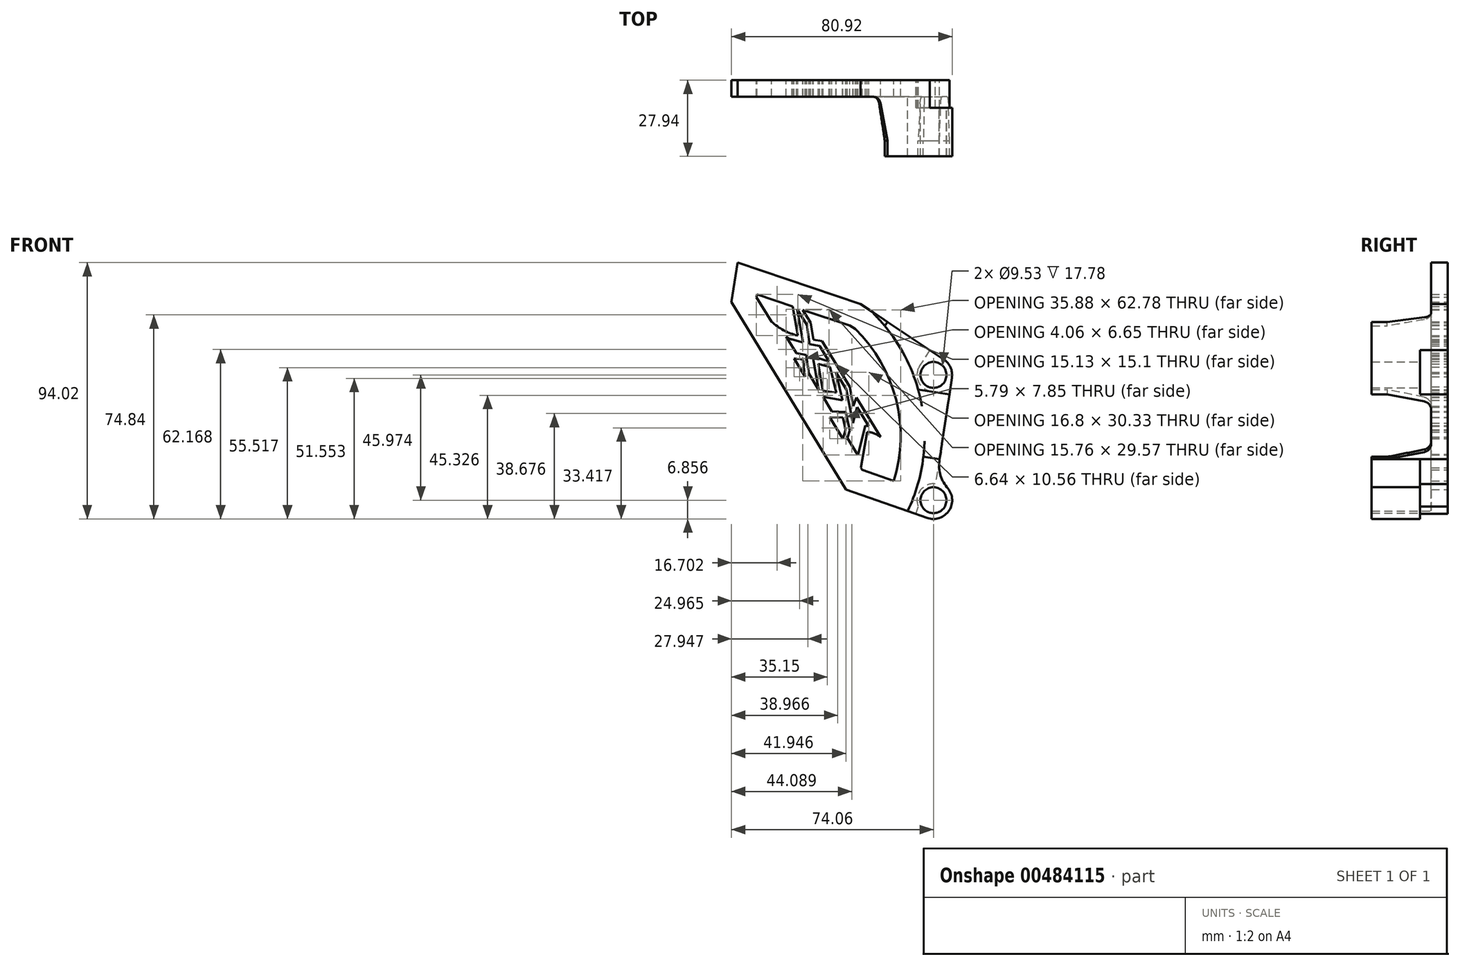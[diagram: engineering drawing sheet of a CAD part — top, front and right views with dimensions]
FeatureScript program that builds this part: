
annotation { "Feature Type Name" : "Feature", "Feature Type Description" : "" }
export const myFeature = defineFeature(function(context is Context, id is Id, definition is map)
    precondition{}
    {
        {
            var Q0;
            Q0=qCreatedBy(makeId("Front.planeOp"),FACE);
            var sketch = newSketch(context, id + "F0", { "sketchPlane" : qUnion([Q0])});
            skCircle(sketch, "E0", {"center": v(0, 0) * mm, "radius": 4.76 * mm});
            skLineSegment(sketch, "E1", {"start": v(0, 40.2) * mm, "end": v(0, -100.93) * mm, "construction": true});
            skCircle(sketch, "E2", {"center": v(0, -45.97) * mm, "radius": 4.76 * mm});
            skCircle(sketch, "E3", {"center": v(0, 0) * mm, "radius": 6.86 * mm});
            skCircle(sketch, "E4", {"center": v(0, -45.97) * mm, "radius": 6.86 * mm});
            skLineSegment(sketch, "E5", {"start": v(0, -45.97) * mm, "end": v(6.94, 0) * mm});
            skLineSegment(sketch, "E6", {"start": v(-32.02, -42.07) * mm, "end": v(-74.06, 26.75) * mm});
            skLineSegment(sketch, "E7", {"start": v(-74.06, 26.75) * mm, "end": v(-71.88, 41.2) * mm});
            skLineSegment(sketch, "E8", {"start": v(-71.88, 41.2) * mm, "end": v(-26.74, 26.02) * mm});
            skArc(sketch, "E9", {"start": v(2.27, -30.95) * mm, "mid": v(2.46, -36.33) * mm, "end": v(4.88, -41.15) * mm});
            skArc(sketch, "E10", {"start": v(-9.46, -49.94) * mm, "mid": v(-4.33, -10.9) * mm, "end": v(-23.2, 23.67) * mm});
            skLineSegment(sketch, "E11", {"start": v(-32.02, -42.07) * mm, "end": v(-9.46, -49.94) * mm});
            skLineSegment(sketch, "E12", {"start": v(-9.46, -49.94) * mm, "end": v(-2.26, -52.45) * mm});
            skLineSegment(sketch, "E13", {"start": v(-26.74, 26.02) * mm, "end": v(-23.2, 23.67) * mm});
            skLineSegment(sketch, "E14", {"start": v(-23.2, 23.67) * mm, "end": v(3.8, 5.71) * mm});
            skLineSegment(sketch, "E15.0", {"start": v(-64.78, 29.56) * mm, "end": v(-30.63, 18.08) * mm});
            skArc(sketch, "E15.1", {"start": v(-14.5, -38.9) * mm, "mid": v(-13.7, -9.04) * mm, "end": v(-28.7, 16.8) * mm});
            skLineSegment(sketch, "E15.2", {"start": v(-26.18, -34.83) * mm, "end": v(-14.5, -38.9) * mm});
            skLineSegment(sketch, "E15.3", {"start": v(-30.63, 18.08) * mm, "end": v(-28.7, 16.8) * mm});
            skLineSegment(sketch, "E15.4", {"start": v(-26.18, -34.83) * mm, "end": v(-64.92, 28.6) * mm});
            skLineSegment(sketch, "E15.5", {"start": v(-64.92, 28.6) * mm, "end": v(-64.78, 29.56) * mm});
            skLineSegment(sketch, "E16.MirrorCS", {"start": v(-27.72, -29.32) * mm, "end": v(-27.63, -29.13) * mm});
            skLineSegment(sketch, "E17.MirrorCS", {"start": v(-25, -18.52) * mm, "end": v(-23.71, -18.84) * mm});
            skLineSegment(sketch, "E18.MirrorCS", {"start": v(-45.43, 11.33) * mm, "end": v(-41.72, 10.68) * mm});
            skLineSegment(sketch, "E19.MirrorCS", {"start": v(-30.66, -20.33) * mm, "end": v(-31.52, -23.1) * mm});
            skLineSegment(sketch, "E20.MirrorCS", {"start": v(-32.2, -20.1) * mm, "end": v(-33.2, -23.37) * mm});
            skLineSegment(sketch, "E21.MirrorCS", {"start": v(-51.14, 6.01) * mm, "end": v(-47.98, 5.65) * mm});
            skArc(sketch, "E22.MirrorCS", {"start": v(-51.91, 13.03) * mm, "mid": v(-53.03, 13.4) * mm, "end": v(-54, 14.07) * mm});
            skLineSegment(sketch, "E23.MirrorCS", {"start": v(-28.25, -8.33) * mm, "end": v(-29.44, -11.4) * mm});
            skLineSegment(sketch, "E24.MirrorCS", {"start": v(-40.9, 12.41) * mm, "end": v(-43.99, 12.95) * mm});
            skLineSegment(sketch, "E25.MirrorCS", {"start": v(-46.67, 7.38) * mm, "end": v(-50.3, 8.01) * mm});
            skLineSegment(sketch, "E26.MirrorCS", {"start": v(-37.87, 2.87) * mm, "end": v(-35.6, -6.56) * mm});
            skLineSegment(sketch, "E27.MirrorCS", {"start": v(-47.98, 5.65) * mm, "end": v(-47.06, -0.67) * mm});
            skLineSegment(sketch, "E28.MirrorCS", {"start": v(-46.45, 18.37) * mm, "end": v(-45.43, 11.33) * mm});
            skLineSegment(sketch, "E29.MirrorCS", {"start": v(-32.26, -13.6) * mm, "end": v(-30.66, -20.33) * mm});
            skLineSegment(sketch, "E30.MirrorCS", {"start": v(-27.63, -29.13) * mm, "end": v(-25, -18.52) * mm});
            skLineSegment(sketch, "E31.MirrorCS", {"start": v(-42.23, 4) * mm, "end": v(-37.87, 2.87) * mm});
            skLineSegment(sketch, "E32.MirrorCS", {"start": v(-42.08, -5.45) * mm, "end": v(-45.66, 0.43) * mm});
            skLineSegment(sketch, "E33.MirrorCS", {"start": v(-37.25, -13.39) * mm, "end": v(-32.26, -13.6) * mm});
            skArc(sketch, "E34.MirrorCS", {"start": v(-49.8, 14.46) * mm, "mid": v(-54.93, 16.37) * mm, "end": v(-59.4, 19.55) * mm});
            skLineSegment(sketch, "E35.MirrorCS", {"start": v(-47.06, -0.67) * mm, "end": v(-38.01, -15.49) * mm});
            skLineSegment(sketch, "E36.MirrorCS", {"start": v(-49.96, 24.12) * mm, "end": v(-46.45, 18.37) * mm});
            skLineSegment(sketch, "E37.MirrorCS", {"start": v(-59.4, 19.55) * mm, "end": v(-51.14, 6.01) * mm});
            skLineSegment(sketch, "E38.MirrorCS", {"start": v(-40.51, -8.05) * mm, "end": v(-37.25, -13.39) * mm});
            skLineSegment(sketch, "E39.MirrorCS", {"start": v(-40.56, -5.69) * mm, "end": v(-42.23, 4) * mm});
            skLineSegment(sketch, "E40.MirrorCS", {"start": v(-47.85, 11.95) * mm, "end": v(-49.96, 24.12) * mm});
            skLineSegment(sketch, "E41.MirrorCS", {"start": v(-33.2, -23.37) * mm, "end": v(-26.63, -34.14) * mm});
            skLineSegment(sketch, "E42.MirrorCS", {"start": v(-29.6, -17.7) * mm, "end": v(-31.96, -5.33) * mm});
            skLineSegment(sketch, "E43.MirrorCS", {"start": v(-29.44, -11.4) * mm, "end": v(-30.7, -4.32) * mm});
            skLineSegment(sketch, "E44.MirrorCS", {"start": v(-52.81, 31.92) * mm, "end": v(-49.8, 14.46) * mm});
            skLineSegment(sketch, "E45.MirrorCS", {"start": v(-35.83, 1) * mm, "end": v(-33.34, -9.3) * mm});
            skLineSegment(sketch, "E46.MirrorCS", {"start": v(-41.72, 10.68) * mm, "end": v(-38.24, 4.97) * mm});
            skLineSegment(sketch, "E47.MirrorCS", {"start": v(-31.52, -23.1) * mm, "end": v(-27.72, -29.32) * mm});
            skLineSegment(sketch, "E48.MirrorCS", {"start": v(-50.3, 8.01) * mm, "end": v(-54, 14.07) * mm});
            skLineSegment(sketch, "E49.MirrorCS", {"start": v(-23.71, -18.84) * mm, "end": v(-28, -11.8) * mm});
            skLineSegment(sketch, "E50.MirrorCS", {"start": v(-51.91, 13.03) * mm, "end": v(-47.85, 11.95) * mm});
            skLineSegment(sketch, "E51.MirrorCS", {"start": v(-31.96, -5.33) * mm, "end": v(-35.83, 1) * mm});
            skLineSegment(sketch, "E52.MirrorCS", {"start": v(-38.01, -15.49) * mm, "end": v(-33.25, -15.7) * mm});
            skLineSegment(sketch, "E53.MirrorCS", {"start": v(-33.34, -9.3) * mm, "end": v(-40.51, -8.05) * mm});
            skArc(sketch, "E54.MirrorCS", {"start": v(-24.31, -20.94) * mm, "mid": v(-21.7, -21.46) * mm, "end": v(-19.4, -22.82) * mm});
            skLineSegment(sketch, "E55.MirrorCS", {"start": v(-43.99, 12.95) * mm, "end": v(-45.02, 19.15) * mm});
            skLineSegment(sketch, "E56.MirrorCS", {"start": v(-44.27, 6.76) * mm, "end": v(-42.08, -5.45) * mm});
            skLineSegment(sketch, "E57.MirrorCS", {"start": v(-35.6, -6.56) * mm, "end": v(-40.56, -5.69) * mm});
            skLineSegment(sketch, "E58.MirrorCS", {"start": v(-19.4, -22.82) * mm, "end": v(-28.25, -8.33) * mm});
            skLineSegment(sketch, "E59.MirrorCS", {"start": v(-28, -11.8) * mm, "end": v(-29.6, -17.7) * mm});
            skLineSegment(sketch, "E60.MirrorCS", {"start": v(-45.02, 19.15) * mm, "end": v(-52.81, 31.92) * mm});
            skLineSegment(sketch, "E61.MirrorCS", {"start": v(-45.66, 0.43) * mm, "end": v(-46.67, 7.38) * mm});
            skLineSegment(sketch, "E62.MirrorCS", {"start": v(-30.7, -4.32) * mm, "end": v(-40.9, 12.41) * mm});
            skLineSegment(sketch, "E63.MirrorCS", {"start": v(-26.63, -34.14) * mm, "end": v(-24.31, -20.94) * mm});
            skLineSegment(sketch, "E64.MirrorCS", {"start": v(-38.24, 4.97) * mm, "end": v(-44.27, 6.76) * mm});
            skLineSegment(sketch, "E65.MirrorCS", {"start": v(-33.25, -15.7) * mm, "end": v(-32.2, -20.1) * mm});
            skSolve(sketch);
        }
        {
            var Q0;
            Q0=makeQuery(id+"F0.imprint","IMPRINT",FACE,{"disambiguationData":[TD([[makeQuery(id+"F0.imprint","IMPRINT",EDGE,{"derivedFrom":sQuery(id+"F0.wireOp",EDGE,"E6")}),-1.0]])]});
            var Q1;
            {var subQ0=sQuery(id+"F0.wireOp",EDGE,"E44.MirrorCS");var subQ1=sQuery(id+"F0.wireOp",EDGE,"E15.0");var subQ2=makeQuery(id+"F0.imprint","INTERSECT",VERTEX,{"derivedFrom":[subQ1,subQ0]});Q1=makeQuery(id+"F0.imprint","IMPRINT",FACE,{"disambiguationData":[TD([[makeQuery(id+"F0.imprint","IMPRINT",EDGE,{"disambiguationData":[TD([[subQ2,-1.0]])],"derivedFrom":subQ1}),1.0]])]});}
            var Q2;
            Q2=makeQuery(id+"F0.imprint","IMPRINT",FACE,{"disambiguationData":[TD([[makeQuery(id+"F0.imprint","IMPRINT",EDGE,{"derivedFrom":sQuery(id+"F0.wireOp",EDGE,"E16.MirrorCS")}),-1.0]])]});
            var Q3;
            {var subQ5=sQuery(id+"F0.wireOp",EDGE,"E35.MirrorCS");Q3=makeQuery(id+"F0.imprint","IMPRINT",FACE,{"disambiguationData":[TD([[makeQuery(id+"F0.imprint","IMPRINT",EDGE,{"derivedFrom":subQ5}),1.0]])]});}
            var Q4;
            {var subQ5=sQuery(id+"F0.wireOp",EDGE,"E41.MirrorCS");Q4=makeQuery(id+"F0.imprint","IMPRINT",FACE,{"disambiguationData":[TD([[makeQuery(id+"F0.imprint","IMPRINT",EDGE,{"derivedFrom":subQ5}),1.0]])]});}
            var Q5;
            {var subQ0=sQuery(id+"F0.wireOp",EDGE,"E37.MirrorCS");Q5=makeQuery(id+"F0.imprint","IMPRINT",FACE,{"disambiguationData":[TD([[makeQuery(id+"F0.imprint","IMPRINT",EDGE,{"derivedFrom":subQ0}),1.0]])]});}
            extrude(context, id + "F1", {"entities" : qUnion([Q0, Q1, Q2, Q3, Q4, Q5]), "depth" : 6.1 * mm, "offsetDistance" : 25.4 * mm});
        }
        {
            var Q0;
            Q0=makeQuery(id+"F0.imprint","IMPRINT",FACE,{"disambiguationData":[TD([[makeQuery(id+"F0.imprint","IMPRINT",EDGE,{"derivedFrom":sQuery(id+"F0.wireOp",EDGE,"E10")}),-1.0]])]});
            var Q1;
            Q1=makeQuery(id+"F0.imprint","IMPRINT",FACE,{"disambiguationData":[TD([[makeQuery(id+"F0.imprint","IMPRINT",EDGE,{"derivedFrom":sQuery(id+"F0.wireOp",EDGE,"E0")}),-1.0]])]});
            var Q2;
            {var subQ0=sQuery(id+"F0.wireOp",EDGE,"E9");var subQ1=sQuery(id+"F0.wireOp",EDGE,"E4");var subQ2=makeQuery(id+"F0.imprint","INTERSECT",VERTEX,{"derivedFrom":[subQ1,subQ0]});Q2=makeQuery(id+"F0.imprint","IMPRINT",FACE,{"disambiguationData":[TD([[makeQuery(id+"F0.imprint","IMPRINT",EDGE,{"disambiguationData":[TD([[subQ2,-1.0]])],"derivedFrom":subQ1}),-1.0]])]});}
            var Q3;
            Q3=makeQuery(id+"F0.imprint","IMPRINT",FACE,{"disambiguationData":[TD([[makeQuery(id+"F0.imprint","IMPRINT",EDGE,{"derivedFrom":sQuery(id+"F0.wireOp",EDGE,"E2")}),-1.0]])]});
            extrude(context, id + "F2", {"entities" : qUnion([Q0, Q1, Q2, Q3]), "operationType" : NewBodyOperationType.ADD, "depth" : 27.94 * mm, "offsetDistance" : 25.4 * mm});
        }
        {
            var Q0;
            {var subQ0=sQuery(id+"F0.wireOp",EDGE,"E10");Q0=makeQuery(id+"F2.boolean.opBoolean","MERGE",FACE,{"derivedFrom":[makeQuery(id+"F1.opExtrude","CAP_FACE",FACE,{"disambiguationData":[OSD([sQuery(id+"F0.wireOp",EDGE,"E6"),sQuery(id+"F0.wireOp",EDGE,"E7"),sQuery(id+"F0.wireOp",EDGE,"E8"),subQ0,sQuery(id+"F0.wireOp",EDGE,"E11"),sQuery(id+"F0.wireOp",EDGE,"E13"),sQuery(id+"F0.wireOp",EDGE,"E15.0"),sQuery(id+"F0.wireOp",EDGE,"E15.1"),sQuery(id+"F0.wireOp",EDGE,"E15.2"),sQuery(id+"F0.wireOp",EDGE,"E15.3"),sQuery(id+"F0.wireOp",EDGE,"E15.4"),sQuery(id+"F0.wireOp",EDGE,"E15.5"),sQuery(id+"F0.wireOp",EDGE,"E16.MirrorCS"),sQuery(id+"F0.wireOp",EDGE,"E17.MirrorCS"),sQuery(id+"F0.wireOp",EDGE,"E18.MirrorCS"),sQuery(id+"F0.wireOp",EDGE,"E19.MirrorCS"),sQuery(id+"F0.wireOp",EDGE,"E20.MirrorCS"),sQuery(id+"F0.wireOp",EDGE,"E21.MirrorCS"),sQuery(id+"F0.wireOp",EDGE,"E22.MirrorCS"),sQuery(id+"F0.wireOp",EDGE,"E23.MirrorCS"),sQuery(id+"F0.wireOp",EDGE,"E24.MirrorCS"),sQuery(id+"F0.wireOp",EDGE,"E25.MirrorCS"),sQuery(id+"F0.wireOp",EDGE,"E26.MirrorCS"),sQuery(id+"F0.wireOp",EDGE,"E27.MirrorCS"),sQuery(id+"F0.wireOp",EDGE,"E28.MirrorCS"),sQuery(id+"F0.wireOp",EDGE,"E29.MirrorCS"),sQuery(id+"F0.wireOp",EDGE,"E30.MirrorCS"),sQuery(id+"F0.wireOp",EDGE,"E31.MirrorCS"),sQuery(id+"F0.wireOp",EDGE,"E32.MirrorCS"),sQuery(id+"F0.wireOp",EDGE,"E33.MirrorCS"),sQuery(id+"F0.wireOp",EDGE,"E34.MirrorCS"),sQuery(id+"F0.wireOp",EDGE,"E36.MirrorCS"),sQuery(id+"F0.wireOp",EDGE,"E38.MirrorCS"),sQuery(id+"F0.wireOp",EDGE,"E39.MirrorCS"),sQuery(id+"F0.wireOp",EDGE,"E40.MirrorCS"),sQuery(id+"F0.wireOp",EDGE,"E42.MirrorCS"),sQuery(id+"F0.wireOp",EDGE,"E43.MirrorCS"),sQuery(id+"F0.wireOp",EDGE,"E44.MirrorCS"),sQuery(id+"F0.wireOp",EDGE,"E45.MirrorCS"),sQuery(id+"F0.wireOp",EDGE,"E46.MirrorCS"),sQuery(id+"F0.wireOp",EDGE,"E47.MirrorCS"),sQuery(id+"F0.wireOp",EDGE,"E48.MirrorCS"),sQuery(id+"F0.wireOp",EDGE,"E49.MirrorCS"),sQuery(id+"F0.wireOp",EDGE,"E50.MirrorCS"),sQuery(id+"F0.wireOp",EDGE,"E51.MirrorCS"),sQuery(id+"F0.wireOp",EDGE,"E52.MirrorCS"),sQuery(id+"F0.wireOp",EDGE,"E53.MirrorCS"),sQuery(id+"F0.wireOp",EDGE,"E54.MirrorCS"),sQuery(id+"F0.wireOp",EDGE,"E55.MirrorCS"),sQuery(id+"F0.wireOp",EDGE,"E56.MirrorCS"),sQuery(id+"F0.wireOp",EDGE,"E57.MirrorCS"),sQuery(id+"F0.wireOp",EDGE,"E58.MirrorCS"),sQuery(id+"F0.wireOp",EDGE,"E59.MirrorCS"),sQuery(id+"F0.wireOp",EDGE,"E60.MirrorCS"),sQuery(id+"F0.wireOp",EDGE,"E61.MirrorCS"),sQuery(id+"F0.wireOp",EDGE,"E62.MirrorCS"),sQuery(id+"F0.wireOp",EDGE,"E63.MirrorCS"),sQuery(id+"F0.wireOp",EDGE,"E64.MirrorCS"),sQuery(id+"F0.wireOp",EDGE,"E65.MirrorCS")])],"isStart":true}),makeQuery(id+"F2.opExtrude","CAP_FACE",FACE,{"disambiguationData":[OSD([sQuery(id+"F0.wireOp",EDGE,"E0"),sQuery(id+"F0.wireOp",EDGE,"E2"),sQuery(id+"F0.wireOp",EDGE,"E3"),sQuery(id+"F0.wireOp",EDGE,"E4"),sQuery(id+"F0.wireOp",EDGE,"E5"),sQuery(id+"F0.wireOp",EDGE,"E9"),subQ0,sQuery(id+"F0.wireOp",EDGE,"E12"),sQuery(id+"F0.wireOp",EDGE,"E14")])],"isStart":true})]});}
            var sketch = newSketch(context, id + "F3", { "sketchPlane" : qUnion([Q0])});
            skCircle(sketch, "E66", {"center": v(0, 0) * mm, "radius": 6.03 * mm});
            skCircle(sketch, "E67", {"center": v(0, -45.97) * mm, "radius": 6.03 * mm});
            skLineSegment(sketch, "E68", {"start": v(1.37, 9.15) * mm, "end": v(5.1, 3.2) * mm});
            skLineSegment(sketch, "E69", {"start": v(1.37, 9.15) * mm, "end": v(-3.8, 5.71) * mm});
            skLineSegment(sketch, "E70", {"start": v(-5.86, -7.16) * mm, "end": v(1.05, -5.94) * mm});
            skLineSegment(sketch, "E71", {"start": v(-5.86, -7.16) * mm, "end": v(-6.78, -1.02) * mm});
            skLineSegment(sketch, "E72", {"start": v(-2.27, -30.95) * mm, "end": v(-0.65, -39.98) * mm});
            skLineSegment(sketch, "E73", {"start": v(6.46, -50.98) * mm, "end": v(5.55, -48.35) * mm});
            skLineSegment(sketch, "E74", {"start": v(6.46, -50.98) * mm, "end": v(2.26, -52.45) * mm});
            skSolve(sketch);
        }
        {
            var Q0;
            {var subQ0=sQuery(id+"F3.wireOp",EDGE,"E67");Q0=makeQuery(id+"F3.imprint","IMPRINT",FACE,{"disambiguationData":[TD([[makeQuery(id+"F3.imprint","IMPRINT",EDGE,{"disambiguationData":[OD(0.0)],"derivedFrom":subQ0}),-1.0]])]});}
            var Q1;
            {var subQ0=sQuery(id+"F3.wireOp",EDGE,"E66");Q1=makeQuery(id+"F3.imprint","IMPRINT",FACE,{"disambiguationData":[TD([[makeQuery(id+"F3.imprint","IMPRINT",EDGE,{"disambiguationData":[OD(0.0)],"derivedFrom":subQ0}),1.0]])]});}
            var Q2;
            {var subQ2=sQuery(id+"F3.wireOp",EDGE,"E70");Q2=makeQuery(id+"F3.imprint","IMPRINT",FACE,{"disambiguationData":[TD([[makeQuery(id+"F3.imprint","IMPRINT",EDGE,{"derivedFrom":subQ2}),1.0]])]});}
            var Q3;
            {var subQ2=sQuery(id+"F3.wireOp",EDGE,"E68");Q3=makeQuery(id+"F3.imprint","IMPRINT",FACE,{"disambiguationData":[TD([[makeQuery(id+"F3.imprint","IMPRINT",EDGE,{"derivedFrom":subQ2}),-1.0]])]});}
            var Q4;
            Q4=makeQuery(id+"F3.imprint","IMPRINT",FACE,{"disambiguationData":[TD([[makeQuery(id+"F3.imprint","IMPRINT",EDGE,{"derivedFrom":makeQuery(id+"F2.opExtrude","CAP_EDGE",EDGE,{"disambiguationData":[OSD([sQuery(id+"F0.wireOp",EDGE,"E2")])],"isStart":true})}),1.0]])]});
            extrude(context, id + "F4", {"entities" : qUnion([Q0, Q1, Q2, Q3, Q4]), "operationType" : NewBodyOperationType.REMOVE, "oppositeDirection" : true, "depth" : 10.16 * mm, "offsetDistance" : 25.4 * mm});
        }
        {
            var Q0;
            Q0=makeQuery(id+"F2.opExtrude","SWEPT_FACE",FACE,{"disambiguationData":[OSD([sQuery(id+"F0.wireOp",EDGE,"E5")])]});
            var sketch = newSketch(context, id + "F5", { "sketchPlane" : qUnion([Q0])});
            skLineSegment(sketch, "E75", {"start": v(-27.94, -30.27) * mm, "end": v(-27.94, -6.14) * mm});
            skLineSegment(sketch, "E76", {"start": v(-27.94, -6.14) * mm, "end": v(-22.23, -6.14) * mm});
            skLineSegment(sketch, "E77", {"start": v(-27.94, -18.2) * mm, "end": v(-6.1, -18.2) * mm, "construction": true});
            skLineSegment(sketch, "E78", {"start": v(-6.1, -18.2) * mm, "end": v(-6.1, -24.48) * mm});
            skLineSegment(sketch, "E79", {"start": v(-6.1, -18.2) * mm, "end": v(-6.1, -11.92) * mm});
            skLineSegment(sketch, "E80", {"start": v(-22.23, -6.14) * mm, "end": v(-8.66, -8.8) * mm});
            skLineSegment(sketch, "E81", {"start": v(-27.94, -30.27) * mm, "end": v(-22.23, -30.27) * mm});
            skLineSegment(sketch, "E82", {"start": v(-22.23, -30.27) * mm, "end": v(-8.66, -27.6) * mm});
            skPoint(sketch, "E83.visualSharp", {"position": v(-6.1, -27.1) * mm});
            skArc(sketch, "E83.filletArc", {"start": v(-8.66, -27.6) * mm, "mid": v(-6.82, -26.5) * mm, "end": v(-6.1, -24.48) * mm});
            skPoint(sketch, "E84.visualSharp", {"position": v(-6.1, -9.31) * mm});
            skArc(sketch, "E84.filletArc", {"start": v(-6.1, -11.92) * mm, "mid": v(-6.82, -9.9) * mm, "end": v(-8.66, -8.8) * mm});
            skSolve(sketch);
        }
        {
            var Q0;
            Q0=makeQuery(id+"F5.imprint","IMPRINT",FACE,{"disambiguationData":[TD([[makeQuery(id+"F5.imprint","IMPRINT",EDGE,{"derivedFrom":sQuery(id+"F5.wireOp",EDGE,"E75")}),-1.0]])]});
            extrude(context, id + "F6", {"entities" : qUnion([Q0]), "operationType" : NewBodyOperationType.REMOVE, "oppositeDirection" : true, "depth" : 25.4 * mm, "offsetDistance" : 25.4 * mm});
        }
        {
            var Q0;
            Q0=makeQuery(id+"F2.boolean.opBoolean","MERGE",FACE,{"derivedFrom":[makeQuery(id+"F1.opExtrude","SWEPT_FACE",FACE,{"disambiguationData":[OSD([sQuery(id+"F0.wireOp",EDGE,"E13")])]}),makeQuery(id+"F2.opExtrude","SWEPT_FACE",FACE,{"disambiguationData":[OSD([sQuery(id+"F0.wireOp",EDGE,"E14")])]})]});
            var sketch = newSketch(context, id + "F7", { "sketchPlane" : qUnion([Q0])});
            skLineSegment(sketch, "E85", {"start": v(-32.43, -27.94) * mm, "end": v(-24.81, -27.94) * mm});
            skLineSegment(sketch, "E86", {"start": v(-24.81, -27.94) * mm, "end": v(-24.81, -22.23) * mm});
            skLineSegment(sketch, "E87", {"start": v(-32.43, -6.1) * mm, "end": v(-32.43, -27.94) * mm});
            skLineSegment(sketch, "E88", {"start": v(-24.81, -22.23) * mm, "end": v(-27.83, -8.58) * mm});
            skLineSegment(sketch, "E89", {"start": v(-30.93, -6.1) * mm, "end": v(-32.43, -6.1) * mm});
            skPoint(sketch, "E90.visualSharp", {"position": v(-28.38, -6.1) * mm});
            skArc(sketch, "E90.filletArc", {"start": v(-27.83, -8.58) * mm, "mid": v(-28.95, -6.8) * mm, "end": v(-30.93, -6.1) * mm});
            skSolve(sketch);
        }
        {
            var Q0;
            Q0=makeQuery(id+"F7.imprint","IMPRINT",FACE,{"disambiguationData":[TD([[makeQuery(id+"F7.imprint","IMPRINT",EDGE,{"derivedFrom":sQuery(id+"F7.wireOp",EDGE,"E85")}),1.0]])]});
            extrude(context, id + "F8", {"entities" : qUnion([Q0]), "operationType" : NewBodyOperationType.REMOVE, "oppositeDirection" : true, "depth" : 25.4 * mm, "offsetDistance" : 25.4 * mm});
        }
    });
